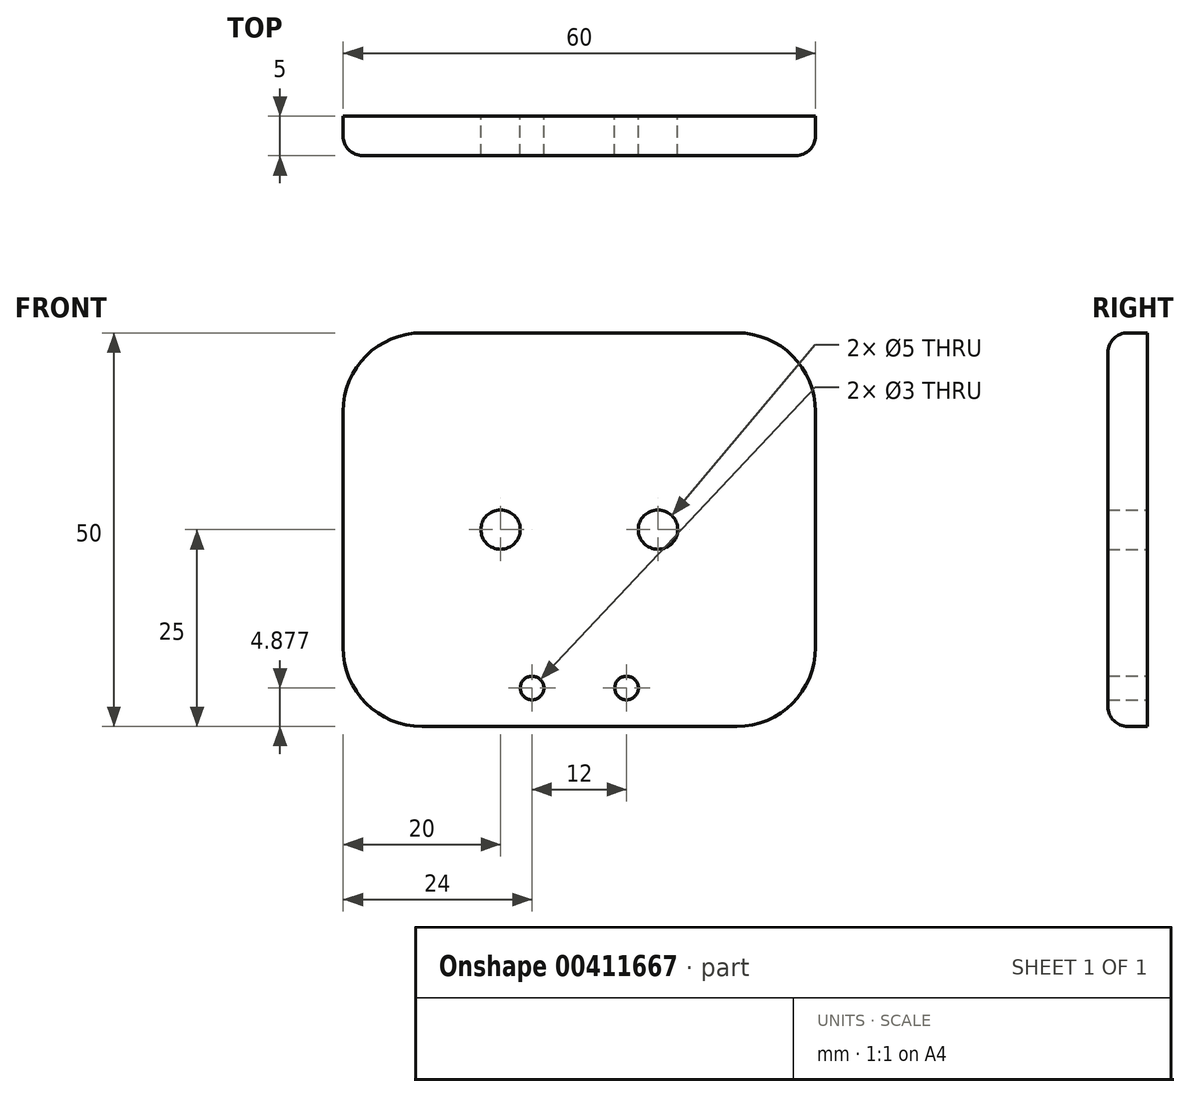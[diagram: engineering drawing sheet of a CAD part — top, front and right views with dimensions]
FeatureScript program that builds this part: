
annotation { "Feature Type Name" : "Feature", "Feature Type Description" : "" }
export const myFeature = defineFeature(function(context is Context, id is Id, definition is map)
    precondition{}
    {
        {
            var Q0;
            Q0=qCreatedBy(makeId("Front.planeOp"),FACE);
            var sketch = newSketch(context, id + "F0", { "sketchPlane" : qUnion([Q0])});
            skLineSegment(sketch, "E0.bottom", {"start": v(20, -25) * mm, "end": v(-20, -25) * mm});
            skLineSegment(sketch, "E0.top", {"start": v(20, 25) * mm, "end": v(-20, 25) * mm});
            skLineSegment(sketch, "E0.left", {"start": v(30, -15) * mm, "end": v(30, 15) * mm});
            skLineSegment(sketch, "E0.right", {"start": v(-30, -15) * mm, "end": v(-30, 15) * mm});
            skPoint(sketch, "E0.middle", {"position": v(0, 0) * mm});
            skLineSegment(sketch, "E1", {"start": v(-47.86, 0) * mm, "end": v(49.53, 0) * mm, "construction": true});
            skLineSegment(sketch, "E2", {"start": v(0, 38.44) * mm, "end": v(0, -48.48) * mm, "construction": true});
            skPoint(sketch, "E2.endSnap0", {"position": v(0, -25) * mm});
            skCircle(sketch, "E3", {"center": v(-10, 0) * mm, "radius": 2.5 * mm});
            skCircle(sketch, "E4.MirrorC", {"center": v(10, 0) * mm, "radius": 2.5 * mm});
            skLineSegment(sketch, "E5", {"start": v(-6, -20.12) * mm, "end": v(7.12, -20.12) * mm, "construction": true});
            skCircle(sketch, "E6", {"center": v(-6, -20.12) * mm, "radius": 1.5 * mm});
            skCircle(sketch, "E7.MirrorC", {"center": v(6, -20.12) * mm, "radius": 1.5 * mm});
            skPoint(sketch, "E8.visualSharp", {"position": v(-30, 25) * mm});
            skArc(sketch, "E8.filletArc", {"start": v(-20, 25) * mm, "mid": v(-27.07, 22.07) * mm, "end": v(-30, 15) * mm});
            skPoint(sketch, "E9.visualSharp", {"position": v(30, 25) * mm});
            skArc(sketch, "E9.filletArc", {"start": v(30, 15) * mm, "mid": v(27.07, 22.07) * mm, "end": v(20, 25) * mm});
            skPoint(sketch, "E10.visualSharp", {"position": v(-30, -25) * mm});
            skArc(sketch, "E10.filletArc", {"start": v(-30, -15) * mm, "mid": v(-27.07, -22.07) * mm, "end": v(-20, -25) * mm});
            skPoint(sketch, "E11.visualSharp", {"position": v(30, -25) * mm});
            skArc(sketch, "E11.filletArc", {"start": v(20, -25) * mm, "mid": v(27.07, -22.07) * mm, "end": v(30, -15) * mm});
            skSolve(sketch);
        }
        {
            var Q0;
            Q0=makeQuery(id+"F0.imprint","IMPRINT",FACE,{"disambiguationData":[TD([[makeQuery(id+"F0.imprint","IMPRINT",EDGE,{"derivedFrom":sQuery(id+"F0.wireOp",EDGE,"E0.bottom")}),-1.0]])]});
            extrude(context, id + "F1", {"entities" : qUnion([Q0]), "depth" : 5 * mm});
        }
        {
            var Q0;
            Q0=makeQuery(id+"F1.opExtrude","CAP_EDGE",EDGE,{"disambiguationData":[OSD([sQuery(id+"F0.wireOp",EDGE,"E0.right")])],"isStart":false});
            var Q1;
            Q1=makeQuery(id+"F1.opExtrude","CAP_EDGE",EDGE,{"disambiguationData":[OSD([sQuery(id+"F0.wireOp",EDGE,"E0.left")])],"isStart":false});
            var Q2;
            Q2=makeQuery(id+"F1.opExtrude","CAP_EDGE",EDGE,{"disambiguationData":[OSD([sQuery(id+"F0.wireOp",EDGE,"E0.top")])],"isStart":false});
            var Q3;
            Q3=makeQuery(id+"F1.opExtrude","CAP_EDGE",EDGE,{"disambiguationData":[OSD([sQuery(id+"F0.wireOp",EDGE,"E0.bottom")])],"isStart":false});
            var Q4;
            Q4=makeQuery(id+"F1.opExtrude","CAP_EDGE",EDGE,{"disambiguationData":[OSD([sQuery(id+"F0.wireOp",EDGE,"E10.filletArc")])],"isStart":false});
            var Q5;
            Q5=makeQuery(id+"F1.opExtrude","CAP_EDGE",EDGE,{"disambiguationData":[OSD([sQuery(id+"F0.wireOp",EDGE,"E11.filletArc")])],"isStart":false});
            var Q6;
            Q6=makeQuery(id+"F1.opExtrude","CAP_EDGE",EDGE,{"disambiguationData":[OSD([sQuery(id+"F0.wireOp",EDGE,"E8.filletArc")])],"isStart":false});
            var Q7;
            Q7=makeQuery(id+"F1.opExtrude","CAP_EDGE",EDGE,{"disambiguationData":[OSD([sQuery(id+"F0.wireOp",EDGE,"E9.filletArc")])],"isStart":false});
            fillet(context, id + "F2", {"entities" : qUnion([Q0, Q1, Q2, Q3, Q4, Q5, Q6, Q7]), "radius" : 2.5 * mm, "tangentPropagation" : true, "allowEdgeOverflow" : false});
        }
    });
